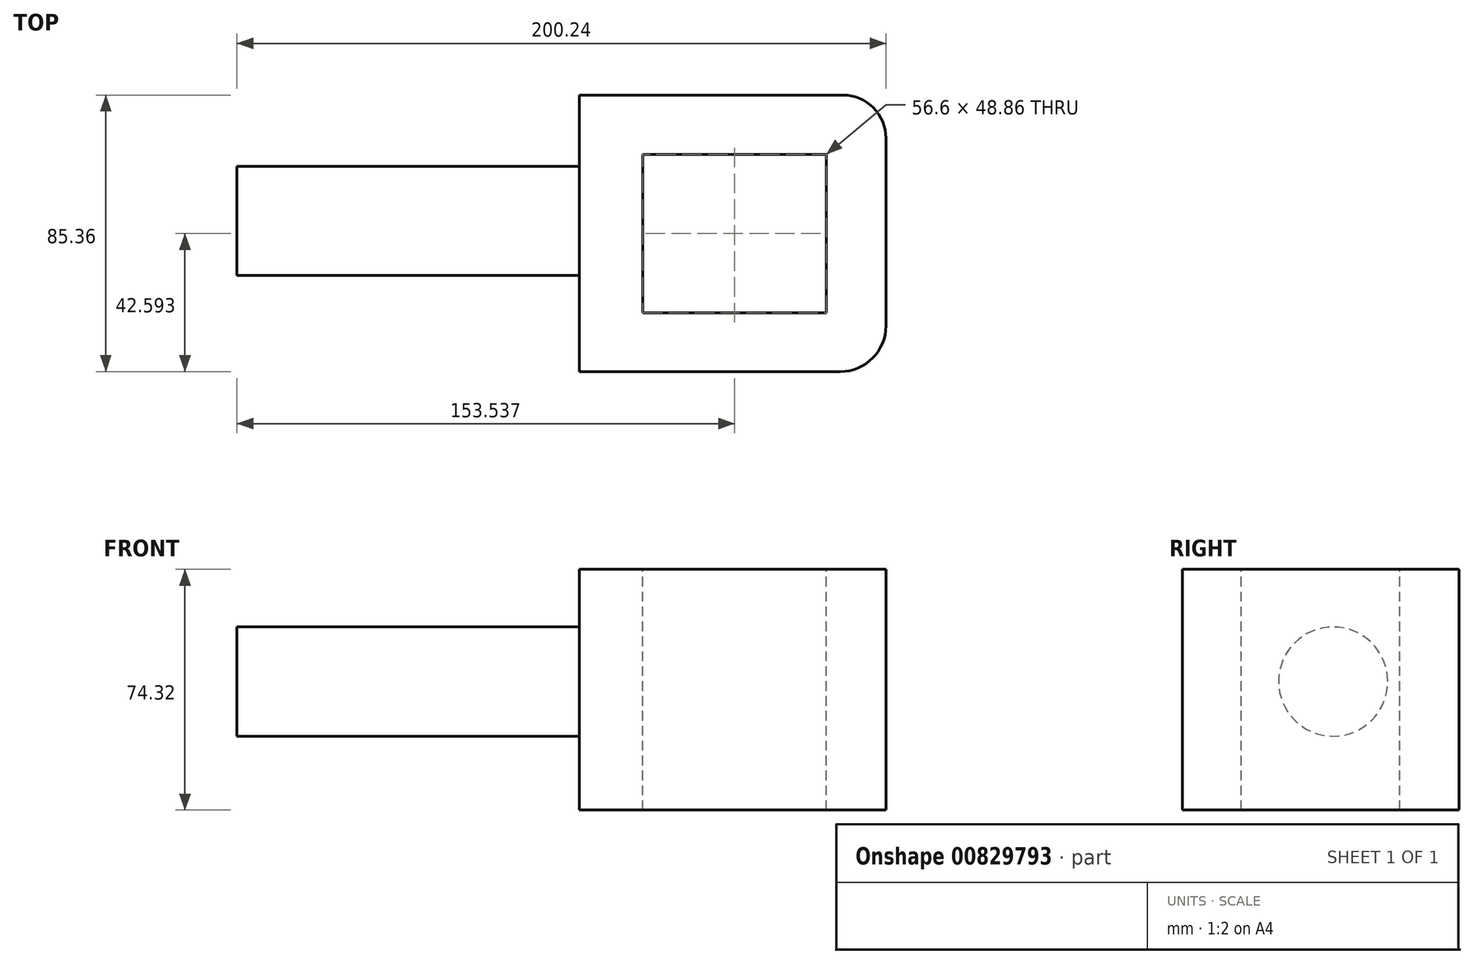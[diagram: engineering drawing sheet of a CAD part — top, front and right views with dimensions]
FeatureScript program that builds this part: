
annotation { "Feature Type Name" : "Feature", "Feature Type Description" : "" }
export const myFeature = defineFeature(function(context is Context, id is Id, definition is map)
    precondition{}
    {
        {
            var Q0;
            Q0=qCreatedBy(makeId("Top.planeOp"),FACE);
            var sketch = newSketch(context, id + "F0", { "sketchPlane" : qUnion([Q0])});
            skLineSegment(sketch, "E0.bottom", {"start": v(-44.22, 38.88) * mm, "end": v(50.4, 38.88) * mm});
            skLineSegment(sketch, "E0.top", {"start": v(-44.22, -46.48) * mm, "end": v(50.4, -46.48) * mm});
            skLineSegment(sketch, "E0.left", {"start": v(-44.22, 38.88) * mm, "end": v(-44.22, -46.48) * mm});
            skLineSegment(sketch, "E0.right", {"start": v(50.4, 38.88) * mm, "end": v(50.4, -46.48) * mm});
            skSolve(sketch);
        }
        {
            var Q0;
            Q0=makeQuery(id+"F0.imprint","IMPRINT",FACE,{"disambiguationData":[TD([[makeQuery(id+"F0.imprint","IMPRINT",EDGE,{"derivedFrom":sQuery(id+"F0.wireOp",EDGE,"E0.bottom")}),-1.0]])]});
            extrude(context, id + "F1", {"entities" : qUnion([Q0]), "depth" : 74.32 * mm, "offsetDistance" : 25.4 * mm});
        }
        {
            var Q0;
            Q0=makeQuery(id+"F1.opExtrude","CAP_FACE",FACE,{"disambiguationData":[OSD([sQuery(id+"F0.wireOp",EDGE,"E0.bottom"),sQuery(id+"F0.wireOp",EDGE,"E0.top"),sQuery(id+"F0.wireOp",EDGE,"E0.left"),sQuery(id+"F0.wireOp",EDGE,"E0.right")])],"isStart":false});
            var sketch = newSketch(context, id + "F2", { "sketchPlane" : qUnion([Q0])});
            skLineSegment(sketch, "E1.bottom", {"start": v(-24.6, 20.54) * mm, "end": v(32, 20.54) * mm});
            skLineSegment(sketch, "E1.top", {"start": v(-24.6, -28.32) * mm, "end": v(32, -28.32) * mm});
            skLineSegment(sketch, "E1.left", {"start": v(-24.6, 20.54) * mm, "end": v(-24.6, -28.32) * mm});
            skLineSegment(sketch, "E1.right", {"start": v(32, 20.54) * mm, "end": v(32, -28.32) * mm});
            skSolve(sketch);
        }
        {
            var Q0;
            Q0=makeQuery(id+"F2.imprint","IMPRINT",FACE,{"disambiguationData":[TD([[makeQuery(id+"F2.imprint","IMPRINT",EDGE,{"derivedFrom":sQuery(id+"F2.wireOp",EDGE,"E1.bottom")}),-1.0]])]});
            extrude(context, id + "F3", {"entities" : qUnion([Q0]), "operationType" : NewBodyOperationType.REMOVE, "oppositeDirection" : true, "depth" : 132.84 * mm, "offsetDistance" : 25.4 * mm});
        }
        {
            var Q0;
            Q0=makeQuery(id+"F1.opExtrude","SWEPT_FACE",FACE,{"disambiguationData":[OSD([sQuery(id+"F0.wireOp",EDGE,"E0.left")])]});
            var sketch = newSketch(context, id + "F4", { "sketchPlane" : qUnion([Q0])});
            skCircle(sketch, "E2", {"center": v(0, 39.67) * mm, "radius": 16.83 * mm});
            skSolve(sketch);
        }
        {
            var Q0;
            Q0=makeQuery(id+"F4.imprint","IMPRINT",FACE,{"disambiguationData":[TD([[makeQuery(id+"F4.imprint","IMPRINT",EDGE,{"derivedFrom":sQuery(id+"F4.wireOp",EDGE,"E2")}),1.0]])]});
            extrude(context, id + "F5", {"entities" : qUnion([Q0]), "operationType" : NewBodyOperationType.ADD, "depth" : 105.62 * mm, "offsetDistance" : 25.4 * mm});
        }
        {
            var Q0;
            Q0=makeQuery(id+"F1.opExtrude","SWEPT_EDGE",EDGE,{"disambiguationData":[OSD([sQuery(id+"F0.wireOp",EDGE,"E0.top"),sQuery(id+"F0.wireOp",EDGE,"E0.right")])]});
            fillet(context, id + "F6", {"entities" : qUnion([Q0]), "radius" : 14.15 * mm, "tangentPropagation" : true, "allowEdgeOverflow" : false});
        }
        {
            var Q0;
            Q0=makeQuery(id+"F1.opExtrude","SWEPT_EDGE",EDGE,{"disambiguationData":[OSD([sQuery(id+"F0.wireOp",EDGE,"E0.bottom"),sQuery(id+"F0.wireOp",EDGE,"E0.right")])]});
            fillet(context, id + "F7", {"entities" : qUnion([Q0]), "radius" : 13.34 * mm, "tangentPropagation" : true, "allowEdgeOverflow" : false});
        }
    });
